# Revit family: Pedro-syst-IT-en
name_source: partatom
category: Electrical Equipment
units: mm (PartAtom-declared; Revit-internal decimal feet)

## family parameters
Cut with Voids When Loaded = No
Host = Face
Panel Configuration = Two Columns, Circuits Across
Part Type = Panelboard
Room Calculation Point = No
Round Connector Dimension = Use Diameter
Shared = No

## types (12) — shared parameters
EF000003 - Mounting method = EV000384 - Surface mounted (plaster)
EF000007 - Colour = EV000270 - Grey
EF000116 - RAL-number = 7035
EF000118 - With mounting plate = No
EF000339 - Type of cover = EV004216 - Door
EF001062 - EMC-version = Yes
EF001088 - Extension possible = Yes
EF001134 - DIN-rail = Yes
EF001596 - Material housing = EV000139 - Plastic
EF004462 - Type of closure = EV000154 - Other
EF005474 - Degree of protection (IP) = EV006422 - IP66
EF006306 - With lock = Yes
EF009212 - Cover model = EV000116 - Closed
EF015776 - Earthing terminal block = No
EF015777 - Neutral terminal block = No
EF015941 - Signal passing door = No
HG000001 - Number of columns = 1
HG000002 - With door or cover = Yes
HG000003 - Range = Pedro
HG000005 - Thickness = 3 mm  [stored 0.00984252 ft]
HG000006 - Flush mounted = No
HG000009 - Double swing door = No
HG000010 - Asymmetric doors = No
HG000011 - Empty rows from bottom = No
Manufacturer = Hager
Type Comments = Pedro
zero-valued in all types: Default Elevation, EF000218 - Built-in depth, EF000332 - Built-in height, EF000846 - Built-in width, HG000007 - Number of empty columns, HG000008 - Number of empty rows

## per-type parameters (varying)
| type | EF000008 - Width | EF000040 - Height | EF000049 - Depth | EF000266 - Number of rows | EF001131 - Internal depth | EF002950 - Width in number of modular spacings | EF006244 - Transparent cover/door | HG000004 - Manufacturer reference | Model |
| Surface mounted IP66 W325 H428.2 D178 12 Modular spacings - B04602 | 325 mm | 428 mm | 178 mm | 3 | 148 mm | 12 | No | B04602 | B04602 |
| Surface mounted IP66 W325 H428.2 D178 12 Modular spacings - B04622 | 325 mm | 428 mm | 178 mm | 3 | 148 mm | 12 | Yes | B04622 | B04622 |
| Surface mounted IP66 W433.5 H503.7 D210 18 Modular spacings - B04603 | 434 mm | 504 mm | 210 mm | 3 | 180 mm | 18 | No | B04603 | B04603 |
| Surface mounted IP66 W433.5 H503.7 D210 18 Modular spacings - B04623 | 434 mm | 504 mm | 210 mm | 3 | 180 mm | 18 | Yes | B04623 | B04623 |
| Surface mounted IP66 W433.5 H653.6 D210 18 Modular spacings - B04604 | 434 mm | 654 mm | 210 mm | 4 | 180 mm | 18 | No | B04604 | B04604 |
| Surface mounted IP66 W433.5 H653.6 D210 18 Modular spacings - B04624 | 434 mm | 654 mm | 210 mm | 4 | 180 mm | 18 | Yes | B04624 | B04624 |
| Surface mounted IP66 W542.4 H654.6 D264.5 24 Modular spacings - B04605 | 542 mm | 655 mm | 264 mm | 4 | 234 mm | 24 | No | B04605 | B04605 |
| Surface mounted IP66 W542.4 H654.6 D264.5 24 Modular spacings - B04625 | 542 mm | 655 mm | 264 mm | 4 | 234 mm | 24 | Yes | B04625 | B04625 |
| Surface mounted IP66 W615.4 H805.6 D318.7 28 Modular spacings - B04606 | 615 mm | 806 mm | 319 mm | 5 | 289 mm | 28 | No | B04606 | B04606 |
| Surface mounted IP66 W615.4 H805.6 D318.7 28 Modular spacings - B04626 | 615 mm | 806 mm | 319 mm | 5 | 289 mm | 28 | Yes | B04626 | B04626 |
| Surface mounted IP66 W810 H1056.2 D355 38 Modular spacings - B04608 | 810 mm | 1056 mm  [stored 3.46457 ft] | 355 mm | 5 | 319 mm | 38 | No | B04608 | B04608 |
| Surface mounted IP66 W810 H1056.2 D355 38 Modular spacings - B04628 | 810 mm | 1056 mm  [stored 3.46457 ft] | 355 mm | 5 | 319 mm | 38 | Yes | B04628 | B04628 |

note: [stored X ft] marks values corroborated as IEEE doubles in the binary element streams (Revit-internal decimal feet)

## geometry (parser evidence)
native form markers: Sweep x12
no freeform markers — native parametric forms only
